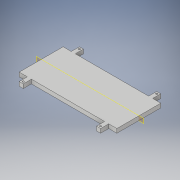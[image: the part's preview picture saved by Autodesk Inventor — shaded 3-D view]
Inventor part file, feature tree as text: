
AUTODESK INVENTOR PART (.ipt)
format: ipt  version: 2018 (Build 220112000, 112)  size: 137,728 bytes
history: native  units: in
note: dims shown in document units (in); Inventor stores cm internally (conversion verified against a paired STEP export)
features: extrude x2, sketch x2, plane x1, mirror x1
ambient origin geometry x8: Origin, YZ Plane, XZ Plane, XY Plane, X Axis, Y Axis, Z Axis, Center Point
bodies: Solid1 (feature_tree)
feature tree (6):
  extrude  "Extrusion1"  Depth=2.7in
  extrude  "Extrusion2"  TaperAngle=0.0deg  [1 undecoded]
  plane  "Work Plane1"
  mirror  "Mirror1"
  sketch  "Sketch1"  dims[d0=6.0in d1=2.7in]
  sketch  "Sketch2"  dims[d2=0.25in d3=0.0in d4=0.5in d5=0.25in d6=0.11in d7=0.125in d8=0.125in d9=0.0in d10=0.5in d11=0.5in d12=0.25in d13=0.11in d14=0.125in d15=0.125in d16=0.0in d17=0.5in d18=0.25in d19=0.0in]
note: 1 required parameter value undecoded (feature->parameter linkage not recoverable at this tier; creation-order binding heuristic only, values carry confidence <= 0.55)
